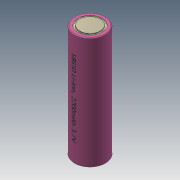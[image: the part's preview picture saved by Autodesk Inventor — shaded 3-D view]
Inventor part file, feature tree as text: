
AUTODESK INVENTOR PART (.ipt)
format: ipt  version: 2015 SP1 (Build 190203100, 203)  size: 865,280 bytes
history: native  units: mm
features: sketch x5, extrude x4, fillet x3, plane x1, emboss x1
ambient origin geometry x8: Origin, YZ Plane, XZ Plane, XY Plane, X Axis, Y Axis, Z Axis, Center Point
bodies: Solid1 (feature_tree)
feature tree (14):
  extrude  "Extrusion1"  Depth=64.7mm TaperAngle=0.0deg
  extrude  "Extrusion2"  Depth=0.1mm TaperAngle=0.0deg
  extrude  "Extrusion3"  Depth=0.1mm TaperAngle=0.0deg
  fillet  "Fillet1"  Radius=0.5mm
  extrude  "Extrusion4"  Depth=12.0mm
  fillet  "Fillet2"  Radius=0.6mm
  fillet  "Fillet3"  Radius=0.5mm
  plane  "Work Plane1"
  emboss  "Emboss1"
  sketch  "Sketch1"  dims[d0=18.0mm d1=64.7mm d2=0.0mm]
  sketch  "Sketch2"  dims[d3=12.0mm d4=0.1mm d5=0.0mm]
  sketch  "Sketch3"  dims[d6=14.0mm d7=0.1mm d8=0.0mm d9=0.5mm]
  sketch  "Sketch4"  dims[d10=14.0mm d11=12.0mm d12=0.6mm d13=0.0mm d14=0.5mm]
  sketch  "Sketch5"  dims[d15=0.1mm d16=-9.0mm d17=55.0mm d18=0.01mm d19=0.0mm]
